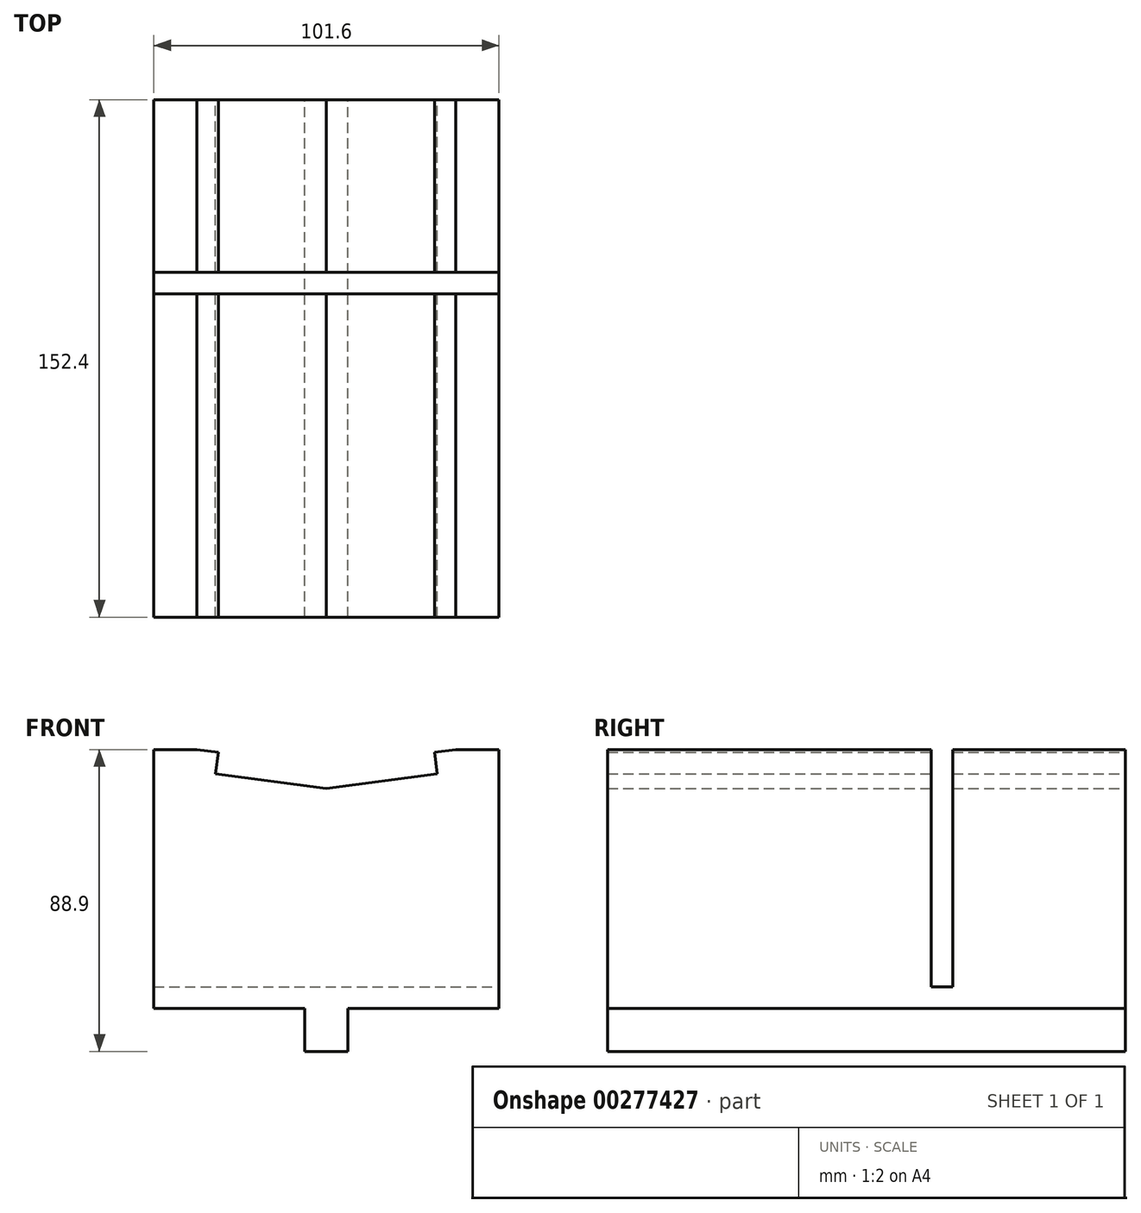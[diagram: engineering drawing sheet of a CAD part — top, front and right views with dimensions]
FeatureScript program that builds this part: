
annotation { "Feature Type Name" : "Feature", "Feature Type Description" : "" }
export const myFeature = defineFeature(function(context is Context, id is Id, definition is map)
    precondition{}
    {
        {
            var Q0;
            Q0=qCreatedBy(makeId("Front.planeOp"),FACE);
            var sketch = newSketch(context, id + "F0", { "sketchPlane" : qUnion([Q0])});
            skLineSegment(sketch, "E0", {"start": v(-6.35, 0) * mm, "end": v(6.35, 0) * mm});
            skLineSegment(sketch, "E1", {"start": v(6.35, 0) * mm, "end": v(6.35, 12.7) * mm});
            skLineSegment(sketch, "E2", {"start": v(6.35, 12.7) * mm, "end": v(50.8, 12.7) * mm});
            skLineSegment(sketch, "E3", {"start": v(50.8, 12.7) * mm, "end": v(50.8, 88.9) * mm});
            skLineSegment(sketch, "E4", {"start": v(50.8, 88.9) * mm, "end": v(38.1, 88.9) * mm});
            skLineSegment(sketch, "E5", {"start": v(38.1, 88.9) * mm, "end": v(31.8, 88.07) * mm});
            skLineSegment(sketch, "E6", {"start": v(-31.8, 88.07) * mm, "end": v(-38.1, 88.9) * mm});
            skLineSegment(sketch, "E7", {"start": v(-38.1, 88.9) * mm, "end": v(-50.8, 88.9) * mm});
            skLineSegment(sketch, "E8", {"start": v(-50.8, 88.9) * mm, "end": v(-50.8, 12.7) * mm});
            skLineSegment(sketch, "E9", {"start": v(-50.8, 12.7) * mm, "end": v(-6.35, 12.7) * mm});
            skLineSegment(sketch, "E10", {"start": v(-6.35, 12.7) * mm, "end": v(-6.35, 0) * mm});
            skLineSegment(sketch, "E11", {"start": v(-74.84, 166.62) * mm, "end": v(-13.73, 166.62) * mm});
            skLineSegment(sketch, "E12", {"start": v(-13.73, 166.62) * mm, "end": v(125.97, 198.37) * mm});
            skLineSegment(sketch, "E13", {"start": v(125.97, 198.37) * mm, "end": v(405.37, 198.37) * mm});
            skLineSegment(sketch, "E14", {"start": v(31.8, 88.07) * mm, "end": v(32.63, 81.78) * mm});
            skLineSegment(sketch, "E15", {"start": v(32.63, 81.78) * mm, "end": v(0, 77.48) * mm});
            skLineSegment(sketch, "E16", {"start": v(0, 77.48) * mm, "end": v(-32.63, 81.78) * mm});
            skLineSegment(sketch, "E17", {"start": v(-32.63, 81.78) * mm, "end": v(-31.8, 88.07) * mm});
            skPoint(sketch, "E18.orphan", {"position": v(0, 83.88) * mm});
            skLineSegment(sketch, "E19", {"start": v(125.97, 198.37) * mm, "end": v(584.76, 302.64) * mm});
            skLineSegment(sketch, "E20", {"start": v(240.27, 224.35) * mm, "end": v(240.27, 166.62) * mm, "construction": true});
            skLineSegment(sketch, "E21", {"start": v(-13.73, 166.62) * mm, "end": v(391.92, 275.31) * mm, "construction": true});
            skLineSegment(sketch, "E22", {"start": v(240.27, 166.62) * mm, "end": v(240.27, 234.68) * mm, "construction": true});
            skSolve(sketch);
        }
        {
            var Q0;
            Q0 = qSketchRegion(id + "F0", true);
            extrude(context, id + "F1", {"entities" : qUnion([Q0]), "depth" : 152.4 * mm});
        }
        {
            var Q0;
            Q0=makeQuery(id+"F1.opExtrude","SWEPT_FACE",FACE,{"disambiguationData":[OSD([sQuery(id+"F0.wireOp",EDGE,"E3")])]});
            var sketch = newSketch(context, id + "F2", { "sketchPlane" : qUnion([Q0])});
            skLineSegment(sketch, "E23.bottom", {"start": v(-57.15, 19.05) * mm, "end": v(-50.8, 19.05) * mm});
            skLineSegment(sketch, "E23.top", {"start": v(-57.15, 95.25) * mm, "end": v(-50.8, 95.25) * mm});
            skLineSegment(sketch, "E23.left", {"start": v(-57.15, 19.05) * mm, "end": v(-57.15, 95.25) * mm});
            skLineSegment(sketch, "E23.right", {"start": v(-50.8, 19.05) * mm, "end": v(-50.8, 95.25) * mm});
            skSolve(sketch);
        }
        {
            var Q0;
            Q0 = qSketchRegion(id + "F2", true);
            extrude(context, id + "F3", {"entities" : qUnion([Q0]), "operationType" : NewBodyOperationType.REMOVE, "endBound" : BoundingType.THROUGH_ALL, "oppositeDirection" : true, "depth" : 25.4 * mm});
        }
    });
